# Revit family: 2Incepa_Boos_Lavatório com Coluna Suspensa_89001
name_source: partatom
category: Plumbing Fixtures
revit_build: Autodesk Revit MEP 2014 (Build: 20131024_2115(x64)
units: mm (PartAtom-declared; Revit-internal decimal feet)

## types (1)
- 01 - Branco
    Assembly Code = D2010400
    CWFU = 0
    Default Elevation = 0 mm  [stored 0 ft]
    Description = Lavatório com coluna suspensa cor branca (89001), 457 x 390 mm, linha Boss - Louças Incepa
    Desenvolvido por = ofcdesk
    Diâmetro Ponto de Esgoto = 40 mm
    HWFU = 0
    Incepa: Categoria = Linhas completas
    Incepa: Cores Disponíveis = Branco
    Incepa: Código = 89001
    Incepa: Descrição = Lavatório com coluna suspensa cor branca (89001), 457 x 390 mm, linha Boss - Louças Incepa
    Incepa: Desenho Técnico = http://www.banheirosincepa.com.br
    Incepa: Fabricante = Incepa
    Incepa: Linha = Boss
    Incepa: Link do Produto = http://www.banheirosincepa.com.br
    Incepa: Norma = ABNT NBR 15097-1: 2011 - Requisitos e métodos de ensaio
    Incepa: Produto = Louças
    Incepa: Tipo = Lavatórios com coluna
    Incepa: Versão = Autodesk Revit MEP 2014
    Manufacturer = Incepa
    Model = 89001
    Raio Ponto de Esgoto = 20 mm
    Selo de Qualidade ofcdesk = Standard
    Tipo de coluna = Celite_City_Coluna para Lavatório_20201 : Suspensa Branco - 20202
    URL = http://www.banheirosincepa.com.br
    WFU = 2

note: [stored X ft] marks values corroborated as IEEE doubles in the binary element streams (Revit-internal decimal feet)

## geometry (parser evidence)
native form markers: Sweep x10
no freeform markers — native parametric forms only
